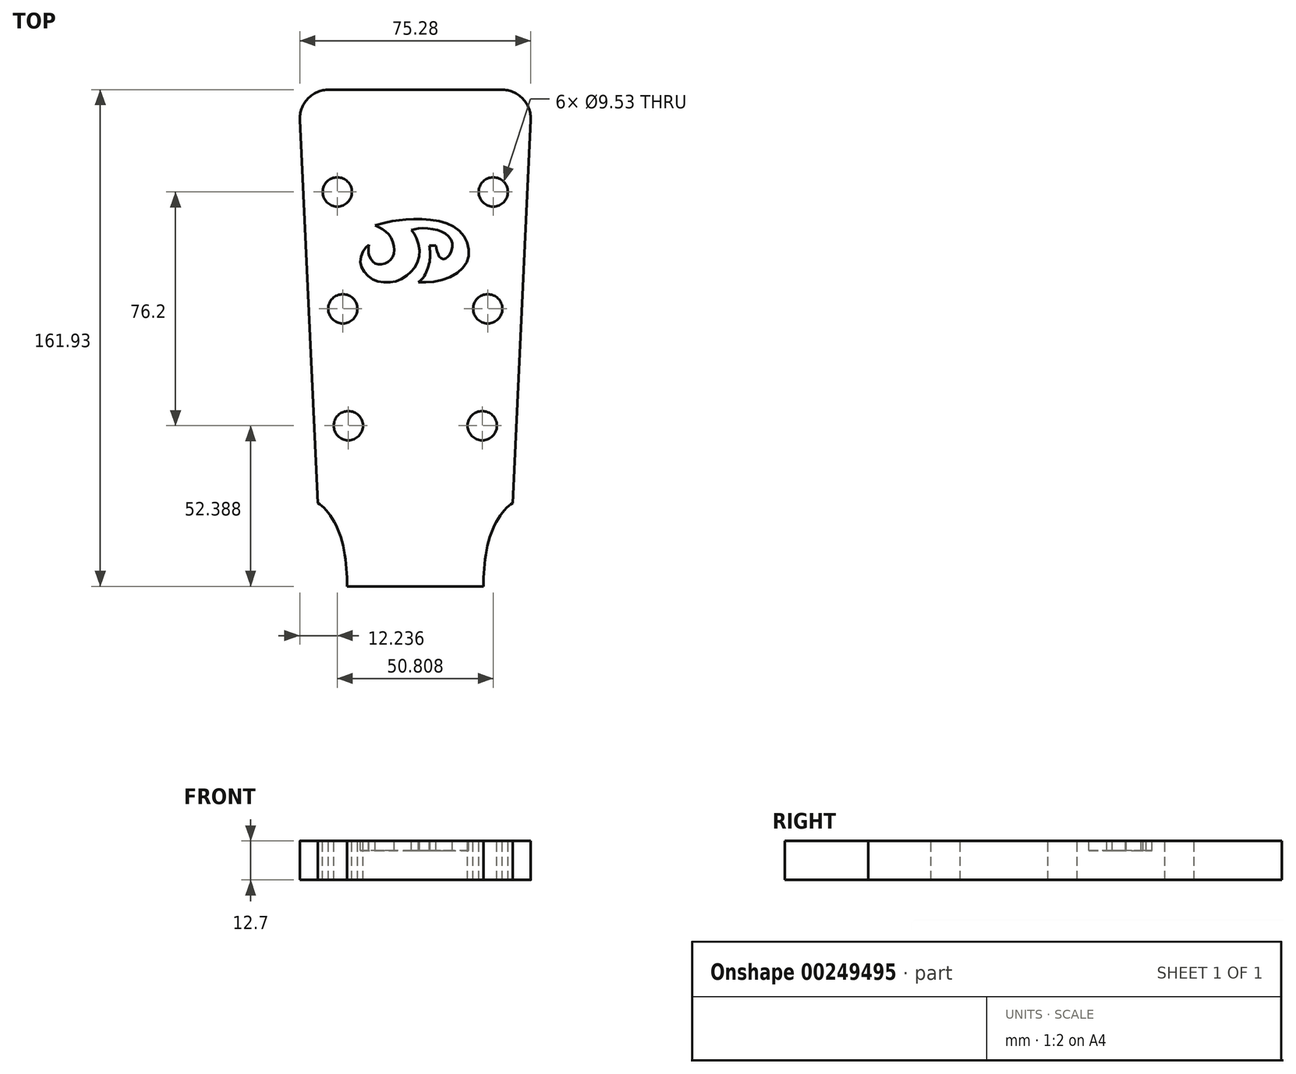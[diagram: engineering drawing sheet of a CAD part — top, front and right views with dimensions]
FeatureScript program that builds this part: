
annotation { "Feature Type Name" : "Feature", "Feature Type Description" : "" }
export const myFeature = defineFeature(function(context is Context, id is Id, definition is map)
    precondition{}
    {
        {
            var Q0;
            Q0=qCreatedBy(makeId("Top.planeOp"),FACE);
            var sketch = newSketch(context, id + "F0", { "sketchPlane" : qUnion([Q0])});
            skFitSpline(sketch, "E0", {"points": [v(-13.03, 117.7) * mm, v(-9.89, 115.95) * mm, v(-7.69, 113.21) * mm, v(-6.9, 109.34) * mm, v(-7.71, 106.94) * mm, v(-9.7, 105.36) * mm, v(-12.1, 105) * mm, v(-13.9, 105.94) * mm, v(-15.07, 107.91) * mm, v(-15.3, 109.64) * mm, v(-15.07, 111.34) * mm], "startDerivative": vector(27.97, -13.26) * mm, "endDerivative": vector(3.87, 20.92) * mm});
            skFitSpline(sketch, "E1", {"points": [v(-15.07, 111.34) * mm, v(-16.35, 110.17) * mm, v(-17.56, 108) * mm, v(-17.8, 105.05) * mm, v(-16.71, 102.62) * mm, v(-14.38, 100.4) * mm, v(-11.62, 99.28) * mm, v(-8, 99.15) * mm, v(-4.9, 100.01) * mm, v(-1.77, 102.16) * mm, v(-0.03, 104.24) * mm, v(1.26, 107.67) * mm, v(1.1, 111.48) * mm, v(-0.2, 114.71) * mm, v(-1.27, 116.17) * mm], "startDerivative": vector(-23.95, -19.14) * mm, "endDerivative": vector(-18.75, 21.8) * mm});
            skFitSpline(sketch, "E2", {"points": [v(-1.27, 116.17) * mm, v(1.04, 116.7) * mm, v(5.33, 116.54) * mm, v(8.87, 115.56) * mm, v(11.43, 113.41) * mm, v(12.1, 110.77) * mm, v(11.08, 108.01) * mm, v(10.2, 107.09) * mm, v(9.15, 106.7) * mm, v(8.08, 107.27) * mm, v(7.53, 108.11) * mm, v(6.94, 109.67) * mm, v(6.69, 111.06) * mm], "startDerivative": vector(25.98, 7.17) * mm, "endDerivative": vector(-1.82, 13.61) * mm});
            skFitSpline(sketch, "E3", {"points": [v(6.69, 111.06) * mm, v(4.59, 111.06) * mm], "startDerivative": vector(-2.1, 0) * mm, "endDerivative": vector(-2.1, 0) * mm});
            skFitSpline(sketch, "E4", {"points": [v(4.59, 111.06) * mm, v(4.82, 108.91) * mm, v(4.47, 105) * mm, v(2.46, 100.5) * mm, v(1.04, 99.15) * mm], "startDerivative": vector(1.34, -9.62) * mm, "endDerivative": vector(-6.49, -5.48) * mm});
            skFitSpline(sketch, "E5", {"points": [v(1.04, 99.15) * mm, v(5.77, 99.3) * mm, v(11.44, 100.91) * mm, v(15.57, 103.88) * mm, v(17.27, 107.07) * mm, v(17.27, 110.7) * mm, v(15.61, 114.56) * mm, v(12.51, 117.3) * mm, v(7.87, 119.04) * mm, v(1.88, 119.7) * mm, v(-3.19, 119.58) * mm, v(-7.17, 119.12) * mm, v(-13.03, 117.7) * mm], "startDerivative": vector(54.2, -1.2) * mm, "endDerivative": vector(-68.78, -18.83) * mm});
            skLineSegment(sketch, "E6", {"start": v(0, 0) * mm, "end": v(0, 172.88) * mm, "construction": true});
            skLineSegment(sketch, "E7", {"start": v(64.24, 109.52) * mm, "end": v(-70.46, 109.52) * mm, "construction": true});
            skLineSegment(sketch, "E8", {"start": v(1.04, 99.15) * mm, "end": v(1.06, 99.15) * mm});
            skSolve(sketch);
        }
        {
            var Q0;
            Q0=qCreatedBy(makeId("Top.planeOp"),FACE);
            var sketch = newSketch(context, id + "F1", { "sketchPlane" : qUnion([Q0])});
            skLineSegment(sketch, "E9", {"start": v(0, 193.54) * mm, "end": v(0, -245.92) * mm, "construction": true});
            skLineSegment(sketch, "E10", {"start": v(0, 161.93) * mm, "end": v(-28.12, 161.93) * mm});
            skLineSegment(sketch, "E11", {"start": v(-37.63, 151.95) * mm, "end": v(-31.75, 27.2) * mm});
            skLineSegment(sketch, "E12", {"start": v(0, 0) * mm, "end": v(-22.23, 0) * mm});
            skPoint(sketch, "E13.visualSharp", {"position": v(-38.1, 161.93) * mm});
            skArc(sketch, "E13.filletArc", {"start": v(-28.12, 161.93) * mm, "mid": v(-35, 158.97) * mm, "end": v(-37.63, 151.95) * mm});
            skLineSegment(sketch, "E14.MirrorCS", {"start": v(0, 0) * mm, "end": v(22.23, 0) * mm});
            skLineSegment(sketch, "E15.MirrorCS", {"start": v(0, 161.93) * mm, "end": v(28.12, 161.93) * mm});
            skLineSegment(sketch, "E16.MirrorCS", {"start": v(37.63, 151.95) * mm, "end": v(31.75, 27.2) * mm});
            skArc(sketch, "E17.MirrorCS", {"start": v(28.12, 161.93) * mm, "mid": v(35, 158.97) * mm, "end": v(37.63, 151.95) * mm});
            skFitSpline(sketch, "E18", {"points": [v(-31.75, 27.2) * mm, v(-25.4, 19.05) * mm, v(-22.23, 0) * mm], "startDerivative": vector(14.73, -8.72) * mm, "endDerivative": vector(-0.26, -31.85) * mm});
            skFitSpline(sketch, "E19.MirrorCS", {"points": [v(31.75, 27.2) * mm, v(25.4, 19.05) * mm, v(22.23, 0) * mm], "startDerivative": vector(-14.73, -8.72) * mm, "endDerivative": vector(0.26, -31.85) * mm});
            skLineSegment(sketch, "E20.0", {"start": v(-22.81, 73.62) * mm, "end": v(-16.63, -57.65) * mm, "construction": true});
            skLineSegment(sketch, "E21", {"start": v(0, 0) * mm, "end": v(-70.02, 0) * mm, "construction": true});
            skCircle(sketch, "E22", {"center": v(-21.81, 52.39) * mm, "radius": 4.76 * mm});
            skCircle(sketch, "E23", {"center": v(-23.6, 90.49) * mm, "radius": 4.76 * mm});
            skCircle(sketch, "E24", {"center": v(-25.4, 128.59) * mm, "radius": 4.76 * mm});
            skCircle(sketch, "E25.MirrorC", {"center": v(25.4, 128.59) * mm, "radius": 4.76 * mm});
            skCircle(sketch, "E26.MirrorC", {"center": v(23.6, 90.49) * mm, "radius": 4.76 * mm});
            skCircle(sketch, "E27.MirrorC", {"center": v(21.81, 52.39) * mm, "radius": 4.76 * mm});
            skCircle(sketch, "E28", {"center": v(-21.81, 52.39) * mm, "radius": 2.38 * mm});
            skCircle(sketch, "E29", {"center": v(-23.6, 90.49) * mm, "radius": 2.38 * mm});
            skCircle(sketch, "E30", {"center": v(-25.4, 128.59) * mm, "radius": 2.38 * mm});
            skCircle(sketch, "E31.MirrorC", {"center": v(21.81, 52.39) * mm, "radius": 2.38 * mm});
            skCircle(sketch, "E32.MirrorC", {"center": v(23.6, 90.49) * mm, "radius": 2.38 * mm});
            skCircle(sketch, "E33.MirrorC", {"center": v(25.4, 128.59) * mm, "radius": 2.38 * mm});
            skSolve(sketch);
        }
        {
            var Q0;
            Q0=makeQuery(id+"F1.imprint","IMPRINT",FACE,{"disambiguationData":[TD([[makeQuery(id+"F1.imprint","IMPRINT",EDGE,{"derivedFrom":sQuery(id+"F1.wireOp",EDGE,"E10")}),1.0]])]});
            var sketch = newSketch(context, id + "F2", { "sketchPlane" : qUnion([Q0])});
            skLineSegment(sketch, "E34.bottom", {"start": v(-22.23, 0) * mm, "end": v(22.23, 0) * mm, "construction": true});
            skLineSegment(sketch, "E34.top", {"start": v(-22.23, -5) * mm, "end": v(22.23, -5) * mm, "construction": true});
            skLineSegment(sketch, "E34.left", {"start": v(-22.23, 0) * mm, "end": v(-22.23, -5) * mm});
            skLineSegment(sketch, "E34.right", {"start": v(22.23, 0) * mm, "end": v(22.23, -5) * mm});
            skLineSegment(sketch, "E35", {"start": v(19.84, 0) * mm, "end": v(19.84, -5) * mm});
            skLineSegment(sketch, "E36", {"start": v(12.1, 0) * mm, "end": v(12.1, -5) * mm});
            skLineSegment(sketch, "E37", {"start": v(5.08, 0) * mm, "end": v(5.08, -5) * mm});
            skLineSegment(sketch, "E38", {"start": v(-18.5, 0) * mm, "end": v(-18.5, -5) * mm});
            skLineSegment(sketch, "E39", {"start": v(-11.47, 0) * mm, "end": v(-11.47, -5) * mm});
            skLineSegment(sketch, "E40", {"start": v(-2.56, 0) * mm, "end": v(-2.56, -5) * mm});
            skLineSegment(sketch, "E41.0", {"start": v(-19.84, 0) * mm, "end": v(-19.84, -5) * mm});
            skLineSegment(sketch, "E42.0", {"start": v(-10.4, 0) * mm, "end": v(-10.4, -5) * mm});
            skLineSegment(sketch, "E43.0", {"start": v(-3.37, 0) * mm, "end": v(-3.37, -5) * mm});
            skLineSegment(sketch, "E44.0", {"start": v(4.47, 0) * mm, "end": v(4.47, -5) * mm});
            skLineSegment(sketch, "E45.0", {"start": v(12.51, 0) * mm, "end": v(12.51, -5) * mm});
            skLineSegment(sketch, "E46.0", {"start": v(19.54, 0) * mm, "end": v(19.54, -5) * mm});
            skLineSegment(sketch, "E47", {"start": v(-19.17, 0) * mm, "end": v(-19.17, -5) * mm, "construction": true});
            skLineSegment(sketch, "E48", {"start": v(-10.94, 0) * mm, "end": v(-10.94, -5) * mm, "construction": true});
            skLineSegment(sketch, "E49", {"start": v(-2.97, 0) * mm, "end": v(-2.97, -5) * mm, "construction": true});
            skLineSegment(sketch, "E50", {"start": v(4.77, 0) * mm, "end": v(4.77, -5) * mm, "construction": true});
            skLineSegment(sketch, "E51", {"start": v(12.3, 0) * mm, "end": v(12.3, -5) * mm, "construction": true});
            skLineSegment(sketch, "E52", {"start": v(19.7, 0) * mm, "end": v(19.7, -5) * mm, "construction": true});
            skSolve(sketch);
        }
        {
            var Q0;
            Q0 = qSketchRegion(id + "F1", true);
            extrude(context, id + "F3", {"entities" : qUnion([Q0]), "oppositeDirection" : true, "depth" : 12.7 * mm});
        }
        {
            var Q0;
            Q0 = qSketchRegion(id + "F0", true);
            extrude(context, id + "F4", {"entities" : qUnion([Q0]), "operationType" : NewBodyOperationType.REMOVE, "oppositeDirection" : true, "depth" : 3.17 * mm});
        }
    });
